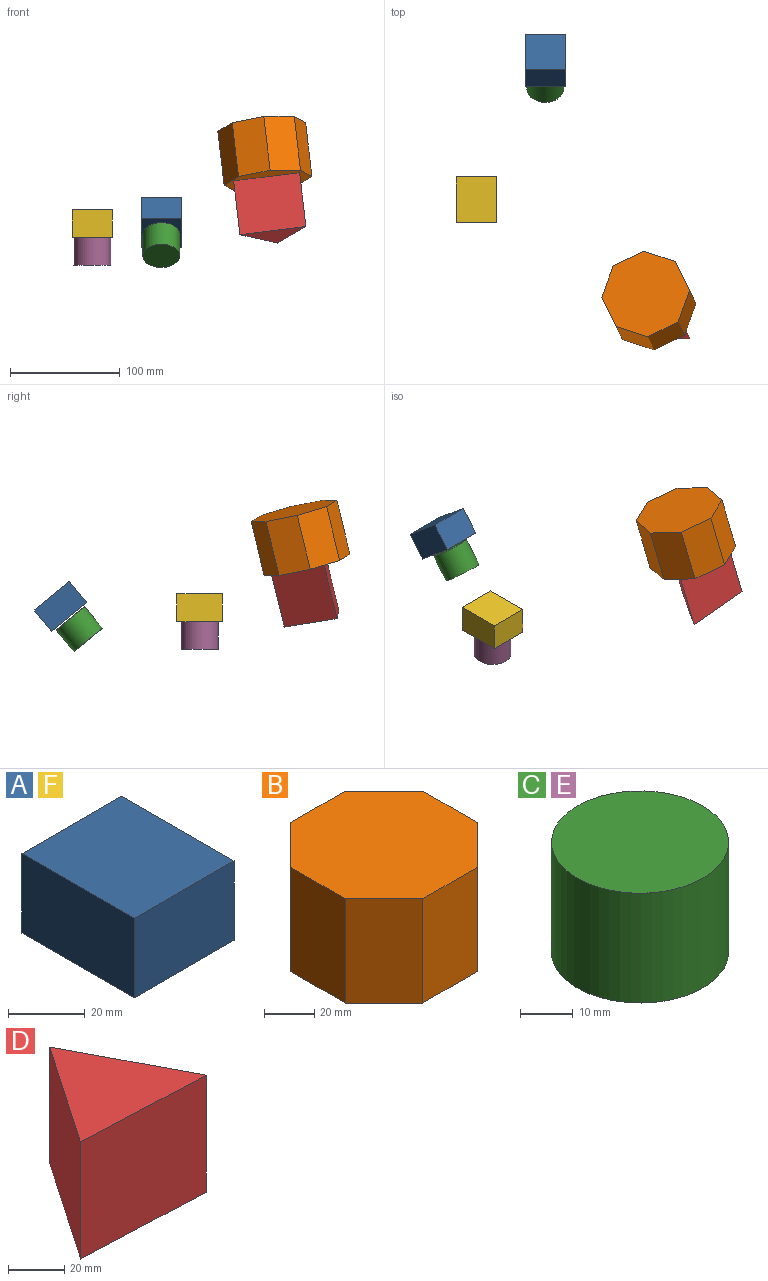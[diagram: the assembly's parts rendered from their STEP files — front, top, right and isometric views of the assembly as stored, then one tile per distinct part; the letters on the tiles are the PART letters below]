
ASSEMBLY  parts=6 mates=3
PART A: 6 faces, bbox 36.8x41.4x25.4 mm
  f0: plane 36.81x25.4mm, normal (0,-1,0), area 935mm2, adj f1,f3,f4,f5
  f1: plane 41.42x25.4mm, normal (1,0,0), area 1052.2mm2, adj f0,f2,f4,f5
  f2: plane 36.81x25.4mm, normal (0,1,0), area 935mm2, adj f1,f3,f4,f5
  f3: plane 41.42x25.4mm, normal (-1,0,0), area 1052.2mm2, adj f0,f2,f4,f5
  f4: plane 41.42x36.81mm, normal (0,0,1), area 1524.9mm2, adj f0,f1,f2,f3
  f5: plane 41.42x36.81mm, normal (0,0,-1), area 1524.9mm2, adj f0,f1,f2,f3
PART B: 10 faces, bbox 74.4x74.4x50.8 mm
  f0: plane 50.8x21.8mm, normal (0.71,-0.71,0), area 1566mm2, adj f1,f7,f8,f9
  f1: plane 50.8x30.83mm, normal (1,0,0), area 1566mm2, adj f0,f2,f8,f9
  f2: plane 50.8x21.8mm, normal (0.71,0.71,0), area 1566mm2, adj f1,f3,f8,f9
  f3: plane 50.8x30.83mm, normal (0,1,0), area 1566mm2, adj f2,f4,f8,f9
  f4: plane 50.8x21.8mm, normal (-0.71,0.71,0), area 1566mm2, adj f3,f5,f8,f9
  f5: plane 50.8x30.83mm, normal (-1,0,0), area 1566mm2, adj f4,f6,f8,f9
  f6: plane 50.8x21.8mm, normal (-0.71,-0.71,0), area 1566mm2, adj f5,f7,f8,f9
  f7: plane 50.8x30.83mm, normal (0,-1,0), area 1566mm2, adj f0,f6,f8,f9
  f8: plane 74.42x74.42mm, normal (0,0,1), area 4588.4mm2, adj f0,f1,f2,f3,f4,f5,f6,f7
  f9: plane 74.42x74.42mm, normal (0,0,-1), area 4588.4mm2, adj f0,f1,f2,f3,f4,f5,f6,f7
PART C: 3 faces, bbox 33.5x33.5x25.4 mm
  f0: cylinder r=16.74mm len=33.48mm, axis (0,0,-1), area 2671.8mm2, adj f1,f2
  f1: plane 33.48x33.48mm, normal (0,0,1), area 880.5mm2, adj f0
  f2: plane 33.48x33.48mm, normal (0,0,-1), area 880.5mm2, adj f0
PART D: 5 faces, bbox 60.5x51.5x50.8 mm
  f0: plane 50.8x49.02mm, normal (-0.83,0.56,0), area 3018mm2, adj f1,f2,f3,f4
  f1: plane 60.52x50.8mm, normal (-0.04,-1,0), area 3077.1mm2, adj f0,f2,f3,f4
  f2: plane 51.47x50.8mm, normal (0.89,0.46,0), area 2951.8mm2, adj f0,f1,f3,f4
  f3: plane 60.52x51.47mm, normal (0,0,1), area 1524.6mm2, adj f0,f1,f2
  f4: plane 60.52x51.47mm, normal (0,0,-1), area 1524.6mm2, adj f0,f1,f2
PART E: same geometry as C
PART F: same geometry as A
PLACE A rot(axis=(1,0,0),140.5deg) t=(62.88,134.85,23.69)mm
PLACE B rot(axis=(0.97,0.22,0.03),165.4deg) t=(169.54,-32.23,89.49)mm
PLACE C rot(axis=(-1,0,0),39.5deg) t=(5.22,53.1,23.22)mm
PLACE D rot(axis=(-0.9,-0.44,0),15deg) t=(120.44,-101.36,-4.8)mm
PLACE E rot(axis=(1,0,0),180deg) t=(-57.66,62.77,0)mm
PLACE F at identity
MATE planar E.f0 <-> F.f5  axis (0,0,1) through (0,0,0)mm
MATE revolute B.f8 <-> D.f3  axis (0.11,-0.23,-0.97) through (160.13,-97.85,51.6)mm
MATE slider A.f4 <-> C.f0  axis (0,-0.64,-0.77) through (62.88,118.69,4.09)mm
